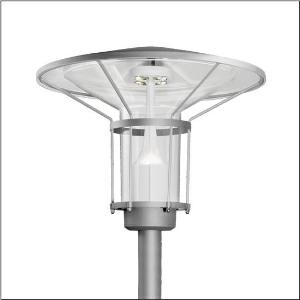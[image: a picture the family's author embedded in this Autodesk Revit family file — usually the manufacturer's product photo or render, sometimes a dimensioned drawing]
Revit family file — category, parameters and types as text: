
# Revit family: laterne_classic_iq___p1_0a_5xa5245lf14h_4a87
name_source: partatom
category: Lighting Fixtures
units: mm (PartAtom-declared; Revit-internal decimal feet)

## family parameters
Cut with Voids When Loaded = No
Host = Face
Light Source = No
Part Type = Normal
Room Calculation Point = No
Round Connector Dimension = Use Diameter
Shared = No

## types (1)
- --- (1 x LED, 1360 lm, 10 W, 4000K)
    Apparent Load = 10 VA
    CIE Flux Codes = 30 61 91 96 100
    Color Rendering = 70
    Color Temperature = 4000K
    Default Elevation = 1800 mm
    Description = Lantern Classic iQ, mast luminaire, Module 540 iQ-SR, primary light control with 3 zone facetted reflector, of plastic, silver coated, highly specular, structured, primary optical cover: cover, of PMMA, transparent, light distribution: P1.0a, light emission: direct distribution, primary light characteristic: strongly asymmetric, installation type: post-top, LED, High Power LED, rated luminous flux: 1.360lm, luminous efficacy: 136lm/W, light colour: 740, colour temperature: 4000K, control gear: ECG iQ, control: presetting dimming logarithmic, Street-Remote, Auto-Match, Temp-Guard, Lumen-Switch, Night-Set, Smart-Wire, Light-Fading, Desk-Remote (wireless, voltage-free reading and setting of iQ features in the workshop via application-optimized NFC function/RFID function), optimised constant luminous flux control (CLO 2.0), with terminal, 6-pole, max. 2.5mm², mains connection: 230..240V, AC, 50/60Hz, start of lifetime: 10W, end of service life: 10W, reduction: 5W, luminaire housing, upper part, of glass-fibre reinforced polyester, coated, Siteco® metallic grey (DB 702S), diameter: 750mm, height: 596mm, spigot size: d x l = 76 x 70mm (post-top) | with reducer (optional accessory) 60 x 70mm, post-top mast mounting element, of diecast aluminium, coated, Siteco® metallic grey (DB 702S), Module 540 iQ-SR, traffic white (RAL 9016), equipment: standard, protection rating (complete): IP65, insulation class (complete): insulation class II (safety insulation), certification: CE, ENEC, VDE, packaging unit: 1 piece

Light Distribution: P1.0a
    Height = 596 mm
    Lamp = 1 x LED
    Lamp Light Flux = 1360 lm
    Lamp Power = 10 W
    Lamp count = 1
    Length = 750 mm
    Luminous efficacy = 136 lm/W
    Manufacturer = Siteco
    ModVariant = No
    Model = 5XA5245LF14H
    Number of Poles = 1
    OnlyDefault = Yes
    Power Factor = 1
    Product Name = Laterne Classic iQ | P1.0a
    Product group = mast luminaire | pylon top
    ProductGroupID = 6100
    Protection Class = Protection class II
    Protection Degree = IP 65
    RLX_Detail_Level = 1
    RLX_Emergency_Light_Flux = 0 lm
    RLX_Emergency_Type = 0
    RLX_Emergency_Type_DB = No
    RlxData = <blob elided: 98233 chars, md5=5cdc51c2>
    Socket = socket
    Standby Power = 0 W
    System Light Flux = 1360 lm
    System Power = 10 W
    Type Comments = factory setting: luminous flux: 100 % | dim-lin: 254 | 401 mA
    Type Image = l_1006052.jpg
    URL = http://relux.com
    VarID = @adj_092537
    Voltage = 0 V
    Weight = 0.00 kg
    Width = 0 mm  [stored 0 ft]

note: [stored X ft] marks values corroborated as IEEE doubles in the binary element streams (Revit-internal decimal feet)

## geometry (parser evidence)
native form markers: Blend x4, Sweep x9
no freeform markers — native parametric forms only
